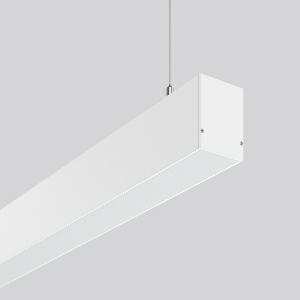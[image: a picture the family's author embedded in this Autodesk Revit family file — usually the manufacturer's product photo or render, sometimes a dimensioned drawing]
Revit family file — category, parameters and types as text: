
# Revit family: less_is_more_50_312311_002_1_ce31
name_source: partatom
category: Lighting Fixtures
units: mm (PartAtom-declared; Revit-internal decimal feet)

## family parameters
Cut with Voids When Loaded = No
Host = Face
Light Source = No
Part Type = Normal
Room Calculation Point = No
Round Connector Dimension = Use Diameter
Shared = No

## types (1)
- LESS IS MORE 50 (1 x LED Modul 840, 2400 lm, 4000)
    Apparent Load = 22 VA
    CIE Flux Codes = 48 79 95 100 100
    Color Rendering = 80
    Color Temperature = 4000
    Default Elevation = 1800 mm
    Description = Series: LESS IS MORE 50
Linear pendant luminaire for aesthetically sophisticated lighting. Housing: extruded aluminium profile, powder-coated. End cap aluminium powder-coated. Canopy made of aluminium, powder-coated. Diffuser made of non-yellowing plastic (PMMA), opal. Direct light emission. Suitable for pendant. 2-point steel cable suspension freely positionable and infinitely height-adjustable. Special lengths available on request. LED unit with integrated converter interchangeable and removable. Suitable for through-wiring. With sensors or as a safety luminaire on request. 
Colour: traffic white, matt (RAL 9016)
Length: 847 mm
Width: 57 mm
Height: 75 mm
Suspension length: 2000 mm
Lamp: LED
Socket: without socket
Colour temperature: 4000K
Colour rendering index (CRI): 80
System power: 22 W
Rated luminous flux: 2400 lm
Luminous efficiency: 109 lm/W
Control gear: Regulated power supply
Protection class: I
Type of protection: IP 20
    Height = 75 mm
    Lamp = 1 x LED Modul 840
    Lamp Light Flux = 2400 lm
    Lamp count = 1
    Length = 847 mm
    Lifetime = 50000 h
    Luminous efficacy = 109 lm/W
    Manufacturer = RZB
    ModVariant = No
    Model = 312311.002.1
    Mounting Place = Ceiling
    Mounting Type = Pendant
    Number of Poles = 1
    OnlyDefault = Yes
    Power Factor = 1
    Product Name = LESS IS MORE 50
    Product group = Pendant LED linear luminaires
    ProductGroupID = 907
    Protection Class = Protection class I
    Protection Degree = IP 20
    RLX_Detail_Level = 1
    RLX_Emergency_Light_Flux = 0 lm
    RLX_Emergency_Type = 0
    RLX_Emergency_Type_DB = No
    RlxData = <blob elided: 20593 chars, md5=4e70070f>
    Socket = socket
    Standby Power = 0 W
    System Light Flux = 2400 lm
    System Power = 22 W
    Type Comments = Product without accessories
    Type Image = 312318.002.jpg
    URL = http://relux.com
    VarID = ---
    Voltage = 230 V
    Voltage Range = 220-240 V
    Weight = 0.00 kg
    Width = 57 mm

## geometry (parser evidence)
native form markers: Blend x4, Sweep x10
no freeform markers — native parametric forms only
